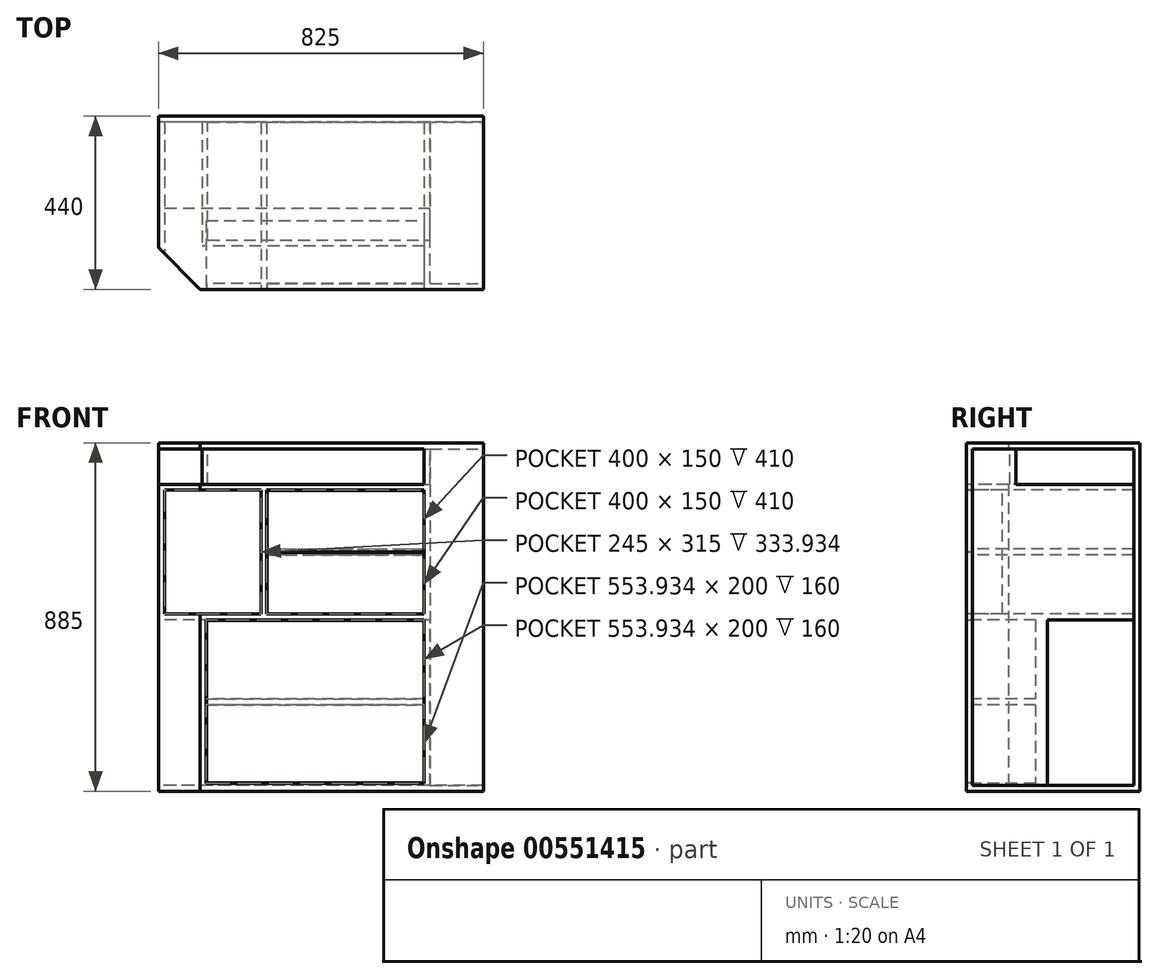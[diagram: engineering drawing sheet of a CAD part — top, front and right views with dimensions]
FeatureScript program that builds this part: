
annotation { "Feature Type Name" : "Feature", "Feature Type Description" : "" }
export const myFeature = defineFeature(function(context is Context, id is Id, definition is map)
    precondition{}
    {
        {
            var Q0;
            Q0=qCreatedBy(makeId("Top.planeOp"),FACE);
            var sketch = newSketch(context, id + "F0", { "sketchPlane" : qUnion([Q0])});
            skLineSegment(sketch, "E0.bottom", {"start": v(0, 0) * mm, "end": v(-825, 0) * mm});
            skLineSegment(sketch, "E0.top", {"start": v(0, -440) * mm, "end": v(-718.93, -440) * mm});
            skLineSegment(sketch, "E0.left", {"start": v(0, 0) * mm, "end": v(0, -440) * mm});
            skLineSegment(sketch, "E0.right", {"start": v(-825, 0) * mm, "end": v(-825, -333.93) * mm});
            skLineSegment(sketch, "E1", {"start": v(-825, -333.93) * mm, "end": v(-718.93, -440) * mm});
            skSolve(sketch);
        }
        {
            var Q0;
            Q0=makeQuery(id+"F0.imprint","IMPRINT",FACE,{"disambiguationData":[TD([[makeQuery(id+"F0.imprint","IMPRINT",EDGE,{"derivedFrom":sQuery(id+"F0.wireOp",EDGE,"E0.bottom")}),1.0]])]});
            extrude(context, id + "F1", {"entities" : qUnion([Q0]), "depth" : 885 * mm, "offsetDistance" : 25 * mm});
        }
        {
            var Q0;
            Q0=makeQuery(id+"F1.opExtrude","SWEPT_FACE",FACE,{"disambiguationData":[OSD([sQuery(id+"F0.wireOp",EDGE,"E0.right")])]});
            var sketch = newSketch(context, id + "F2", { "sketchPlane" : qUnion([Q0])});
            skLineSegment(sketch, "E2.bottom", {"start": v(15, 15) * mm, "end": v(235, 15) * mm});
            skLineSegment(sketch, "E2.top", {"start": v(15, 435) * mm, "end": v(235, 435) * mm});
            skLineSegment(sketch, "E2.left", {"start": v(15, 15) * mm, "end": v(15, 435) * mm});
            skLineSegment(sketch, "E2.right", {"start": v(235, 15) * mm, "end": v(235, 435) * mm});
            skSolve(sketch);
        }
        {
            var Q0;
            Q0 = qSketchRegion(id + "F2", true);
            extrude(context, id + "F3", {"entities" : qUnion([Q0]), "operationType" : NewBodyOperationType.REMOVE, "oppositeDirection" : true, "depth" : 800 * mm, "offsetDistance" : 25 * mm});
        }
        {
            var Q0;
            Q0=makeQuery(id+"F1.opExtrude","SWEPT_FACE",FACE,{"disambiguationData":[OSD([sQuery(id+"F0.wireOp",EDGE,"E0.top")])]});
            var sketch = newSketch(context, id + "F4", { "sketchPlane" : qUnion([Q0])});
            skLineSegment(sketch, "E3.bottom", {"start": v(-550, 600) * mm, "end": v(-150, 600) * mm});
            skLineSegment(sketch, "E3.top", {"start": v(-550, 450) * mm, "end": v(-150, 450) * mm});
            skLineSegment(sketch, "E3.left", {"start": v(-550, 600) * mm, "end": v(-550, 450) * mm});
            skLineSegment(sketch, "E3.right", {"start": v(-150, 600) * mm, "end": v(-150, 450) * mm});
            skLineSegment(sketch, "E4.bottom", {"start": v(-550, 615) * mm, "end": v(-150, 615) * mm});
            skLineSegment(sketch, "E4.top", {"start": v(-550, 765) * mm, "end": v(-150, 765) * mm});
            skLineSegment(sketch, "E4.left", {"start": v(-550, 615) * mm, "end": v(-550, 765) * mm});
            skLineSegment(sketch, "E4.right", {"start": v(-150, 615) * mm, "end": v(-150, 765) * mm});
            skLineSegment(sketch, "E5.bottom", {"start": v(-565, 765) * mm, "end": v(-810, 765) * mm});
            skLineSegment(sketch, "E5.top", {"start": v(-565, 450) * mm, "end": v(-810, 450) * mm});
            skLineSegment(sketch, "E5.left", {"start": v(-565, 765) * mm, "end": v(-565, 450) * mm});
            skLineSegment(sketch, "E5.right", {"start": v(-810, 765) * mm, "end": v(-810, 450) * mm});
            skSolve(sketch);
        }
        {
            var Q0;
            Q0=makeQuery(id+"F4.imprint","IMPRINT",FACE,{"disambiguationData":[TD([[makeQuery(id+"F4.imprint","IMPRINT",EDGE,{"derivedFrom":sQuery(id+"F4.wireOp",EDGE,"E4.bottom")}),1.0]])]});
            var Q1;
            Q1=makeQuery(id+"F4.imprint","IMPRINT",FACE,{"disambiguationData":[TD([[makeQuery(id+"F4.imprint","IMPRINT",EDGE,{"derivedFrom":sQuery(id+"F4.wireOp",EDGE,"E3.bottom")}),-1.0]])]});
            var Q2;
            {var subQ0=sQuery(id+"F4.wireOp",EDGE,"E5.left");Q2=makeQuery(id+"F4.imprint","IMPRINT",FACE,{"disambiguationData":[TD([[makeQuery(id+"F4.imprint","IMPRINT",EDGE,{"derivedFrom":subQ0}),-1.0]])]});}
            var Q3;
            {var subQ0=sQuery(id+"F4.wireOp",EDGE,"E5.right");Q3=makeQuery(id+"F4.imprint","IMPRINT",FACE,{"disambiguationData":[TD([[makeQuery(id+"F4.imprint","IMPRINT",EDGE,{"derivedFrom":subQ0}),1.0]])]});}
            extrude(context, id + "F5", {"entities" : qUnion([Q0, Q1, Q2, Q3]), "operationType" : NewBodyOperationType.REMOVE, "oppositeDirection" : true, "depth" : 425 * mm, "offsetDistance" : 25 * mm});
        }
        {
            var Q0;
            Q0=makeQuery(id+"F4.imprint","IMPRINT",FACE,{"disambiguationData":[TD([[makeQuery(id+"F4.imprint","IMPRINT",EDGE,{"derivedFrom":sQuery(id+"F4.wireOp",EDGE,"E3.bottom")}),1.0]])]});
            var sketch = newSketch(context, id + "F6", { "sketchPlane" : qUnion([Q0])});
            skLineSegment(sketch, "E6.bottom", {"start": v(-703.93, 435) * mm, "end": v(-150, 435) * mm});
            skLineSegment(sketch, "E6.top", {"start": v(-703.93, 235) * mm, "end": v(-150, 235) * mm});
            skLineSegment(sketch, "E6.left", {"start": v(-703.93, 435) * mm, "end": v(-703.93, 235) * mm});
            skLineSegment(sketch, "E6.right", {"start": v(-150, 435) * mm, "end": v(-150, 235) * mm});
            skLineSegment(sketch, "E7.bottom", {"start": v(-703.93, 220) * mm, "end": v(-150, 220) * mm});
            skLineSegment(sketch, "E7.top", {"start": v(-703.93, 20) * mm, "end": v(-150, 20) * mm});
            skLineSegment(sketch, "E7.left", {"start": v(-703.93, 220) * mm, "end": v(-703.93, 20) * mm});
            skLineSegment(sketch, "E7.right", {"start": v(-150, 220) * mm, "end": v(-150, 20) * mm});
            skSolve(sketch);
        }
        {
            var Q0;
            Q0=makeQuery(id+"F6.imprint","IMPRINT",FACE,{"disambiguationData":[TD([[makeQuery(id+"F6.imprint","IMPRINT",EDGE,{"derivedFrom":sQuery(id+"F6.wireOp",EDGE,"E6.bottom")}),-1.0]])]});
            var Q1;
            Q1=makeQuery(id+"F6.imprint","IMPRINT",FACE,{"disambiguationData":[TD([[makeQuery(id+"F6.imprint","IMPRINT",EDGE,{"derivedFrom":sQuery(id+"F6.wireOp",EDGE,"E7.bottom")}),-1.0]])]});
            extrude(context, id + "F7", {"entities" : qUnion([Q0, Q1]), "operationType" : NewBodyOperationType.REMOVE, "oppositeDirection" : true, "depth" : 175 * mm, "offsetDistance" : 25 * mm});
        }
        {
            var Q0;
            Q0=makeQuery(id+"F1.opExtrude","CAP_FACE",FACE,{"disambiguationData":[OSD([sQuery(id+"F0.wireOp",EDGE,"E0.bottom"),sQuery(id+"F0.wireOp",EDGE,"E0.top"),sQuery(id+"F0.wireOp",EDGE,"E0.left"),sQuery(id+"F0.wireOp",EDGE,"E0.right"),sQuery(id+"F0.wireOp",EDGE,"E1")])],"isStart":false});
            cPlane(context, id + "F8", {"entities" : qUnion([Q0]), "cplaneType" : CPlaneType.OFFSET, "offset" : 15 * mm, "oppositeDirection" : true, "width" : 150 * mm, "height" : 150 * mm});
        }
        {
            var Q0;
            Q0=qCreatedBy(id+"F8.planeOp",FACE);
            var sketch = newSketch(context, id + "F9", { "sketchPlane" : qUnion([Q0])});
            skLineSegment(sketch, "E8.top", {"start": v(-150, -330) * mm, "end": v(-715, -330) * mm});
            skLineSegment(sketch, "E8.right", {"start": v(-715, -15) * mm, "end": v(-715, -330) * mm});
            skLineSegment(sketch, "E9.bottom", {"start": v(-715, -15) * mm, "end": v(-825, -15) * mm});
            skLineSegment(sketch, "E9.top", {"start": v(-150, -440) * mm, "end": v(-825, -440) * mm});
            skLineSegment(sketch, "E9.right", {"start": v(-825, -15) * mm, "end": v(-825, -440) * mm});
            skLineSegment(sketch, "E10", {"start": v(-150, -330) * mm, "end": v(-150, -440) * mm});
            skLineSegment(sketch, "E11.bottom", {"start": v(-700, -315) * mm, "end": v(-15, -315) * mm});
            skLineSegment(sketch, "E11.top", {"start": v(-700, -15) * mm, "end": v(-15, -15) * mm});
            skLineSegment(sketch, "E11.left", {"start": v(-700, -315) * mm, "end": v(-700, -15) * mm});
            skLineSegment(sketch, "E11.right", {"start": v(-15, -315) * mm, "end": v(-15, -15) * mm});
            skSolve(sketch);
        }
        {
            var Q0;
            Q0 = qSketchRegion(id + "F9", true);
            extrude(context, id + "F10", {"entities" : qUnion([Q0]), "operationType" : NewBodyOperationType.REMOVE, "oppositeDirection" : true, "depth" : 90 * mm, "offsetDistance" : 25 * mm});
        }
        {
            var Q0;
            Q0=makeQuery(id+"F4.imprint","IMPRINT",FACE,{"disambiguationData":[TD([[makeQuery(id+"F4.imprint","IMPRINT",EDGE,{"derivedFrom":sQuery(id+"F4.wireOp",EDGE,"E3.bottom")}),1.0]])]});
            var sketch = newSketch(context, id + "F11", { "sketchPlane" : qUnion([Q0])});
            skLineSegment(sketch, "E12.bottom", {"start": v(-150, 615) * mm, "end": v(-550, 615) * mm});
            skLineSegment(sketch, "E12.top", {"start": v(-150, 600) * mm, "end": v(-550, 600) * mm});
            skLineSegment(sketch, "E12.left", {"start": v(-150, 615) * mm, "end": v(-150, 600) * mm});
            skLineSegment(sketch, "E12.right", {"start": v(-550, 615) * mm, "end": v(-550, 600) * mm});
            skLineSegment(sketch, "E13.bottom", {"start": v(-150, 235) * mm, "end": v(-703.93, 235) * mm});
            skLineSegment(sketch, "E13.top", {"start": v(-150, 220) * mm, "end": v(-703.93, 220) * mm});
            skLineSegment(sketch, "E13.left", {"start": v(-150, 235) * mm, "end": v(-150, 220) * mm});
            skLineSegment(sketch, "E13.right", {"start": v(-703.93, 235) * mm, "end": v(-703.93, 220) * mm});
            skSolve(sketch);
        }
        {
            var Q0;
            Q0 = qSketchRegion(id + "F11", true);
            extrude(context, id + "F12", {"entities" : qUnion([Q0]), "operationType" : NewBodyOperationType.REMOVE, "oppositeDirection" : true, "depth" : 15 * mm, "offsetDistance" : 25 * mm});
        }
        {
            var Q0;
            Q0=makeQuery(id+"F1.opExtrude","SWEPT_FACE",FACE,{"disambiguationData":[OSD([sQuery(id+"F0.wireOp",EDGE,"E0.top")])]});
            var sketch = newSketch(context, id + "F13", { "sketchPlane" : qUnion([Q0])});
            skLineSegment(sketch, "E14.bottom", {"start": v(-549, 764) * mm, "end": v(-151, 764) * mm});
            skLineSegment(sketch, "E14.top", {"start": v(-549, 608) * mm, "end": v(-151, 608) * mm});
            skLineSegment(sketch, "E14.left", {"start": v(-549, 764) * mm, "end": v(-549, 608) * mm});
            skLineSegment(sketch, "E14.right", {"start": v(-151, 764) * mm, "end": v(-151, 608) * mm});
            skLineSegment(sketch, "E15.bottom", {"start": v(-549, 607) * mm, "end": v(-151, 607) * mm});
            skLineSegment(sketch, "E15.top", {"start": v(-549, 451) * mm, "end": v(-151, 451) * mm});
            skLineSegment(sketch, "E15.left", {"start": v(-549, 607) * mm, "end": v(-549, 451) * mm});
            skLineSegment(sketch, "E15.right", {"start": v(-151, 607) * mm, "end": v(-151, 451) * mm});
            skLineSegment(sketch, "E16.bottom", {"start": v(-151, 434) * mm, "end": v(-702.93, 434) * mm});
            skLineSegment(sketch, "E16.top", {"start": v(-151, 21) * mm, "end": v(-702.93, 21) * mm});
            skLineSegment(sketch, "E16.left", {"start": v(-151, 434) * mm, "end": v(-151, 21) * mm});
            skLineSegment(sketch, "E16.right", {"start": v(-702.93, 434) * mm, "end": v(-702.93, 21) * mm});
            skSolve(sketch);
        }
        {
            var Q0;
            Q0 = qSketchRegion(id + "F13", true);
            extrude(context, id + "F14", {"entities" : qUnion([Q0]), "oppositeDirection" : true, "depth" : 15 * mm, "offsetDistance" : 25 * mm});
        }
        {
            var Q0;
            Q0=makeQuery(id+"F1.opExtrude","SWEPT_FACE",FACE,{"disambiguationData":[OSD([sQuery(id+"F0.wireOp",EDGE,"E0.left")])]});
            var sketch = newSketch(context, id + "F15", { "sketchPlane" : qUnion([Q0])});
            skLineSegment(sketch, "E17.bottom", {"start": v(-425, 870) * mm, "end": v(-15, 870) * mm});
            skLineSegment(sketch, "E17.top", {"start": v(-425, 15) * mm, "end": v(-15, 15) * mm});
            skLineSegment(sketch, "E17.left", {"start": v(-425, 870) * mm, "end": v(-425, 15) * mm});
            skLineSegment(sketch, "E17.right", {"start": v(-15, 870) * mm, "end": v(-15, 15) * mm});
            skSolve(sketch);
        }
        {
            var Q0;
            Q0=makeQuery(id+"F15.imprint","IMPRINT",FACE,{"disambiguationData":[TD([[makeQuery(id+"F15.imprint","IMPRINT",EDGE,{"derivedFrom":sQuery(id+"F15.wireOp",EDGE,"E17.bottom")}),-1.0]])]});
            extrude(context, id + "F16", {"entities" : qUnion([Q0]), "operationType" : NewBodyOperationType.REMOVE, "oppositeDirection" : true, "depth" : 135 * mm, "offsetDistance" : 25 * mm});
        }
    });
